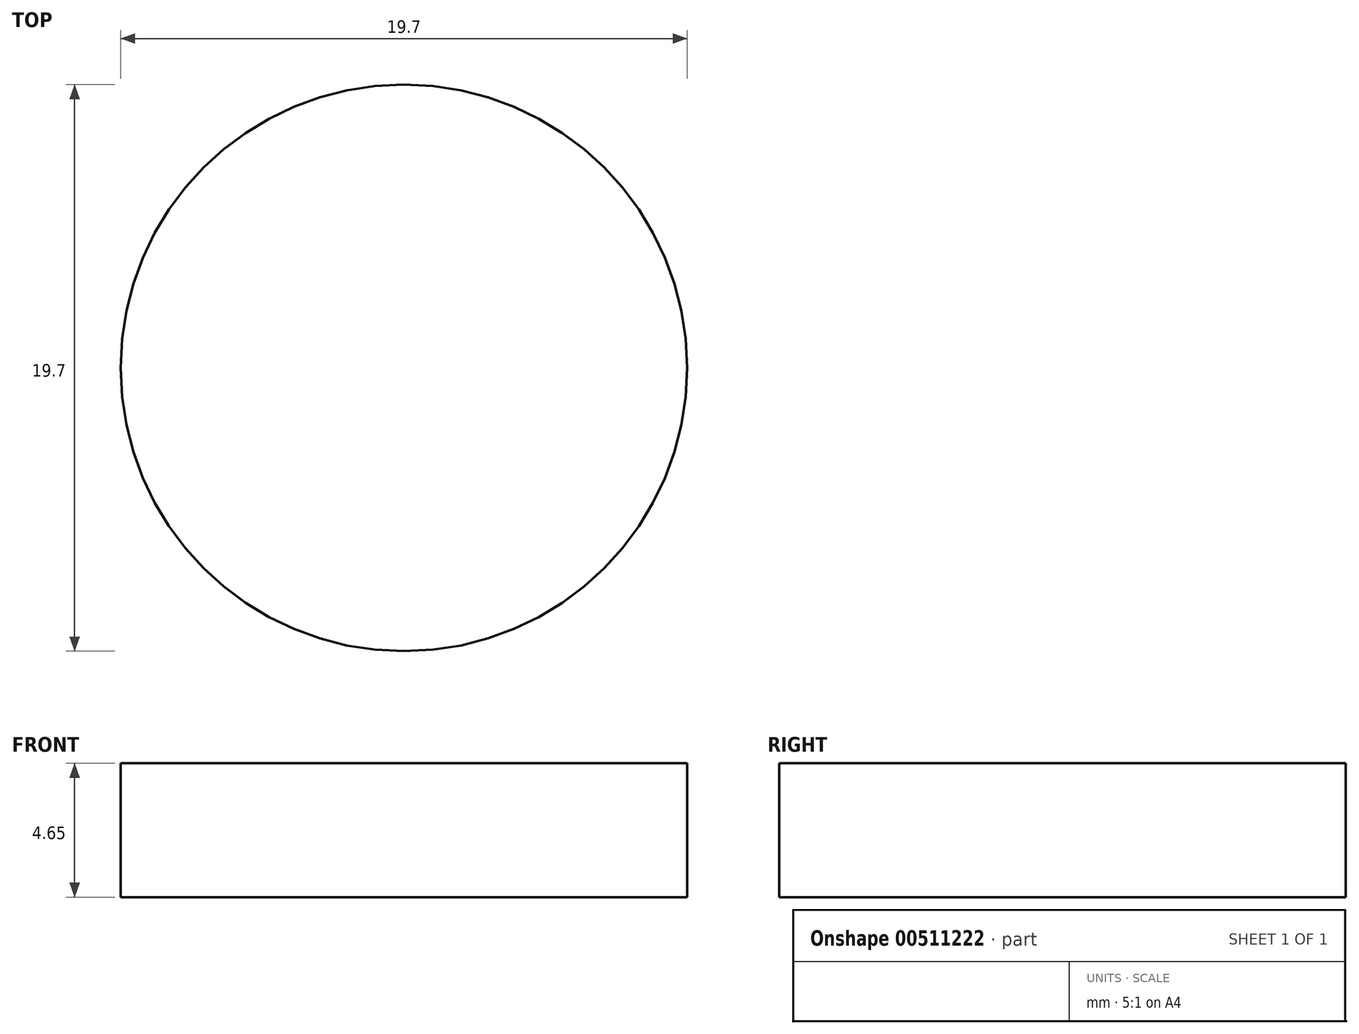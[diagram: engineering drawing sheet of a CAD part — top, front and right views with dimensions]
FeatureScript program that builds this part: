
annotation { "Feature Type Name" : "Feature", "Feature Type Description" : "" }
export const myFeature = defineFeature(function(context is Context, id is Id, definition is map)
    precondition{}
    {
        {
            var Q0;
            Q0=qCreatedBy(makeId("Top.planeOp"),FACE);
            var sketch = newSketch(context, id + "F0", { "sketchPlane" : qUnion([Q0])});
            skCircle(sketch, "E0", {"center": v(0, 0) * mm, "radius": 9.85 * mm});
            skSolve(sketch);
        }
        {
            var Q0;
            Q0 = qSketchRegion(id + "F0", true);
            extrude(context, id + "F1", {"entities" : qUnion([Q0]), "depth" : 4.65 * mm});
        }
    });
